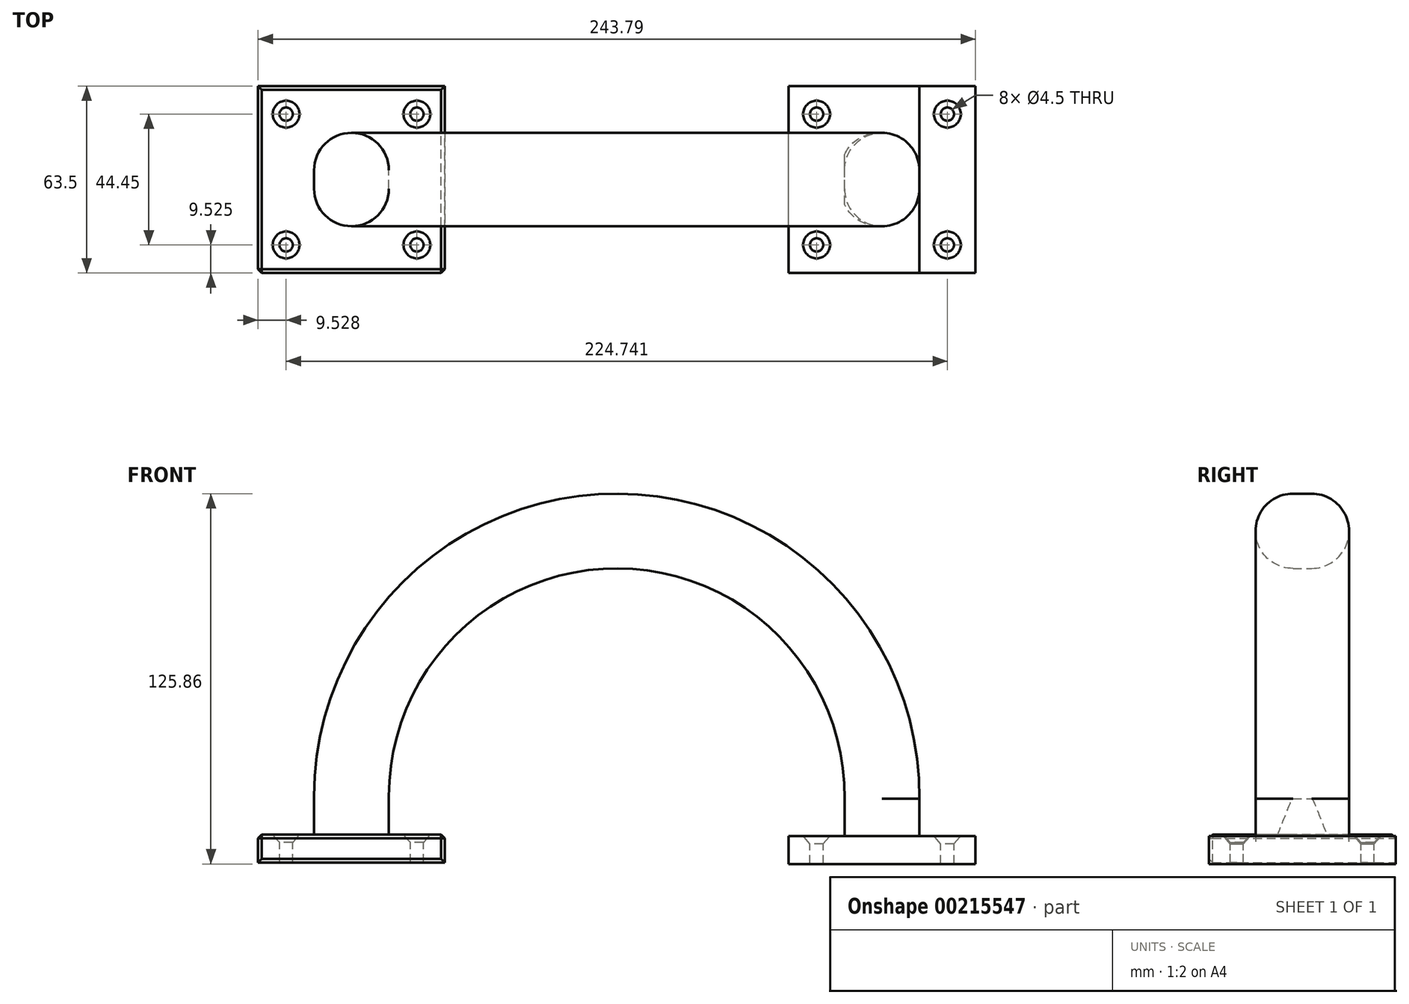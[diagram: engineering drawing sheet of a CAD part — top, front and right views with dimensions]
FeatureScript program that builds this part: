
annotation { "Feature Type Name" : "Feature", "Feature Type Description" : "" }
export const myFeature = defineFeature(function(context is Context, id is Id, definition is map)
    precondition{}
    {
        {
            var Q0;
            Q0=qCreatedBy(makeId("Front.planeOp"),FACE);
            var sketch = newSketch(context, id + "F0", { "sketchPlane" : qUnion([Q0])});
            skLineSegment(sketch, "E0.bottom", {"start": v(-58.67, -4.76) * mm, "end": v(-122.17, -4.76) * mm});
            skLineSegment(sketch, "E0.top", {"start": v(-58.67, 4.76) * mm, "end": v(-122.17, 4.76) * mm});
            skLineSegment(sketch, "E0.left", {"start": v(-58.67, -4.76) * mm, "end": v(-58.67, 4.76) * mm});
            skLineSegment(sketch, "E0.right", {"start": v(-122.17, -4.76) * mm, "end": v(-122.17, 4.76) * mm});
            skLineSegment(sketch, "E1.bottom", {"start": v(121.62, -5.16) * mm, "end": v(58.12, -5.16) * mm});
            skLineSegment(sketch, "E1.top", {"start": v(121.62, 4.37) * mm, "end": v(58.12, 4.37) * mm});
            skLineSegment(sketch, "E1.left", {"start": v(121.62, -5.16) * mm, "end": v(121.62, 4.37) * mm});
            skLineSegment(sketch, "E1.right", {"start": v(58.12, -5.16) * mm, "end": v(58.12, 4.37) * mm});
            skLineSegment(sketch, "E2", {"start": v(-77.72, 4.76) * mm, "end": v(-77.72, 17.85) * mm});
            skLineSegment(sketch, "E3", {"start": v(77.17, 4.37) * mm, "end": v(77.17, 17.07) * mm});
            skArc(sketch, "E4", {"start": v(-77.72, 17.85) * mm, "mid": v(0.12, 95.3) * mm, "end": v(77.17, 17.07) * mm});
            skLineSegment(sketch, "E5.0", {"start": v(102.57, 4.35) * mm, "end": v(102.57, 16.96) * mm});
            skArc(sketch, "E5.1", {"start": v(-103.12, 17.85) * mm, "mid": v(0.18, 120.7) * mm, "end": v(102.57, 16.96) * mm});
            skLineSegment(sketch, "E5.2", {"start": v(-103.12, 4.76) * mm, "end": v(-103.12, 17.85) * mm});
            skLineSegment(sketch, "E6", {"start": v(-103.12, 4.76) * mm, "end": v(-77.72, 4.76) * mm});
            skLineSegment(sketch, "E7", {"start": v(77.17, 4.37) * mm, "end": v(102.57, 4.35) * mm});
            skPoint(sketch, "E8", {"position": v(-86.5, -521.13) * mm});
            skPoint(sketch, "E9", {"position": v(-115.18, -521.13) * mm});
            skSolve(sketch);
        }
        {
            var Q0;
            Q0=makeQuery(id+"F0.imprint","IMPRINT",FACE,{"disambiguationData":[TD([[makeQuery(id+"F0.imprint","IMPRINT",EDGE,{"derivedFrom":sQuery(id+"F0.wireOp",EDGE,"E0.bottom")}),-1.0]])]});
            var Q1;
            Q1=makeQuery(id+"F0.imprint","IMPRINT",FACE,{"disambiguationData":[TD([[makeQuery(id+"F0.imprint","IMPRINT",EDGE,{"derivedFrom":sQuery(id+"F0.wireOp",EDGE,"E1.bottom")}),-1.0]])]});
            extrude(context, id + "F1", {"entities" : qUnion([Q0, Q1]), "endBound" : BoundingType.SYMMETRIC, "depth" : 63.5 * mm});
        }
        {
            var Q0;
            Q0=makeQuery(id+"F0.imprint","IMPRINT",FACE,{"disambiguationData":[TD([[makeQuery(id+"F0.imprint","IMPRINT",EDGE,{"derivedFrom":sQuery(id+"F0.wireOp",EDGE,"E2")}),1.0]])]});
            extrude(context, id + "F2", {"entities" : qUnion([Q0]), "operationType" : NewBodyOperationType.ADD, "endBound" : BoundingType.SYMMETRIC, "depth" : 31.75 * mm});
        }
        {
            var Q0;
            Q0=makeQuery(id+"F1.opExtrude","SWEPT_FACE",FACE,{"disambiguationData":[OSD([sQuery(id+"F0.wireOp",EDGE,"E0.top"),sQuery(id+"F0.wireOp",EDGE,"E6")])]});
            cPlane(context, id + "F3", {"entities" : qUnion([Q0]), "cplaneType" : CPlaneType.OFFSET, "offset" : 0 * mm, "width" : 152.4 * mm, "height" : 152.4 * mm});
        }
        {
            var Q0;
            Q0=qCreatedBy(id+"F3.planeOp",FACE);
            var sketch = newSketch(context, id + "F4", { "sketchPlane" : qUnion([Q0])});
            skCircle(sketch, "E10", {"center": v(-112.64, 22.23) * mm, "radius": 2.8 * mm});
            skCircle(sketch, "E11", {"center": v(-112.64, -22.23) * mm, "radius": 2.8 * mm});
            skCircle(sketch, "E12", {"center": v(-68.2, -22.23) * mm, "radius": 2.8 * mm});
            skCircle(sketch, "E13", {"center": v(-68.2, 22.23) * mm, "radius": 2.8 * mm});
            skCircle(sketch, "E14", {"center": v(67.65, 22.23) * mm, "radius": 2.8 * mm});
            skCircle(sketch, "E15", {"center": v(67.65, -22.23) * mm, "radius": 2.8 * mm});
            skCircle(sketch, "E16", {"center": v(112.1, -22.23) * mm, "radius": 2.8 * mm});
            skCircle(sketch, "E17", {"center": v(112.1, 22.23) * mm, "radius": 2.8 * mm});
            skSolve(sketch);
        }
        {
            var Q0;
            Q0=sQuery(id+"F4.wireOp",VERTEX,"E11.center");
            var Q1;
            Q1=sQuery(id+"F4.wireOp",VERTEX,"E12.center");
            var Q2;
            Q2=sQuery(id+"F4.wireOp",VERTEX,"E13.center");
            var Q3;
            Q3=sQuery(id+"F4.wireOp",VERTEX,"E10.center");
            var Q4;
            Q4=sQuery(id+"F4.wireOp",VERTEX,"E14.center");
            var Q5;
            Q5=sQuery(id+"F4.wireOp",VERTEX,"E17.center");
            var Q6;
            Q6=sQuery(id+"F4.wireOp",VERTEX,"E16.center");
            var Q7;
            Q7=sQuery(id+"F4.wireOp",VERTEX,"E15.center");
            var Q8;
            Q8=makeQuery(id+"F1.opExtrude","SWEPT_BODY",BODY,{"disambiguationData":[OSD([sQuery(id+"F0.wireOp",EDGE,"E0.bottom"),sQuery(id+"F0.wireOp",EDGE,"E0.top"),sQuery(id+"F0.wireOp",EDGE,"E0.left"),sQuery(id+"F0.wireOp",EDGE,"E0.right"),sQuery(id+"F0.wireOp",EDGE,"E6")])]});
            var Q9;
            Q9=makeQuery(id+"F1.opExtrude","SWEPT_BODY",BODY,{"disambiguationData":[OSD([sQuery(id+"F0.wireOp",EDGE,"E1.bottom"),sQuery(id+"F0.wireOp",EDGE,"E1.top"),sQuery(id+"F0.wireOp",EDGE,"E1.left"),sQuery(id+"F0.wireOp",EDGE,"E1.right"),sQuery(id+"F0.wireOp",EDGE,"E5.0"),sQuery(id+"F0.wireOp",EDGE,"E7")])]});
            hole(context, id + "F5", {"style" : HoleStyle.C_SINK, "endStyle" : HoleEndStyle.THROUGH, "standardTappedOrClearance" : lookupTablePath({ "standard" : "ANSI", "fit" : "Normal (ASME)", "size" : "#8", "type" : "Clearance" }), "standardBlindInLast" : lookupTablePath({ "fit" : "Free", "standard" : "ANSI", "size" : "#8", "type" : "Clearance" }), "holeDiameter" : 4.5 * mm, "cSinkDiameter" : 9.12 * mm, "cSinkAngle" : 82 * degree, "locations" : qUnion([Q0, Q1, Q2, Q3, Q4, Q5, Q6, Q7]), "scope" : qUnion([Q8, Q9]), "isTappedThrough" : true});
        }
        {
            var Q0;
            Q0=makeQuery(id+"F1.opExtrude","CAP_EDGE",EDGE,{"disambiguationData":[OSD([sQuery(id+"F0.wireOp",EDGE,"E0.top"),sQuery(id+"F0.wireOp",EDGE,"E6")])],"isStart":true});
            var Q1;
            Q1=makeQuery(id+"F1.opExtrude","SWEPT_EDGE",EDGE,{"disambiguationData":[OSD([sQuery(id+"F0.wireOp",EDGE,"E0.top"),sQuery(id+"F0.wireOp",EDGE,"E0.right")])]});
            var Q2;
            Q2=makeQuery(id+"F1.opExtrude","SWEPT_EDGE",EDGE,{"disambiguationData":[OSD([sQuery(id+"F0.wireOp",EDGE,"E0.top"),sQuery(id+"F0.wireOp",EDGE,"E0.left")])]});
            var Q3;
            Q3=makeQuery(id+"F1.opExtrude","CAP_FACE",FACE,{"disambiguationData":[OSD([sQuery(id+"F0.wireOp",EDGE,"E0.bottom"),sQuery(id+"F0.wireOp",EDGE,"E0.top"),sQuery(id+"F0.wireOp",EDGE,"E0.left"),sQuery(id+"F0.wireOp",EDGE,"E0.right"),sQuery(id+"F0.wireOp",EDGE,"E6")])],"isStart":false});
            chamfer(context, id + "F6", {"entities" : qUnion([Q0, Q1, Q2, Q3]), "width" : 1.27 * mm, "tangentPropagation" : true});
        }
        {
            var Q0;
            Q0=makeQuery(id+"F2.opExtrude","CAP_EDGE",EDGE,{"disambiguationData":[OSD([sQuery(id+"F0.wireOp",EDGE,"E5.1")])],"isStart":false});
            var Q1;
            Q1=makeQuery(id+"F2.opExtrude","CAP_EDGE",EDGE,{"disambiguationData":[OSD([sQuery(id+"F0.wireOp",EDGE,"E4")])],"isStart":false});
            var Q2;
            Q2=makeQuery(id+"F2.opExtrude","CAP_EDGE",EDGE,{"disambiguationData":[OSD([sQuery(id+"F0.wireOp",EDGE,"E4")])],"isStart":true});
            var Q3;
            Q3=makeQuery(id+"F2.opExtrude","CAP_EDGE",EDGE,{"disambiguationData":[OSD([sQuery(id+"F0.wireOp",EDGE,"E5.1")])],"isStart":true});
            fillet(context, id + "F7", {"entities" : qUnion([Q0, Q1, Q2, Q3]), "radius" : 12.7 * mm, "tangentPropagation" : true, "allowEdgeOverflow" : false});
        }
    });
